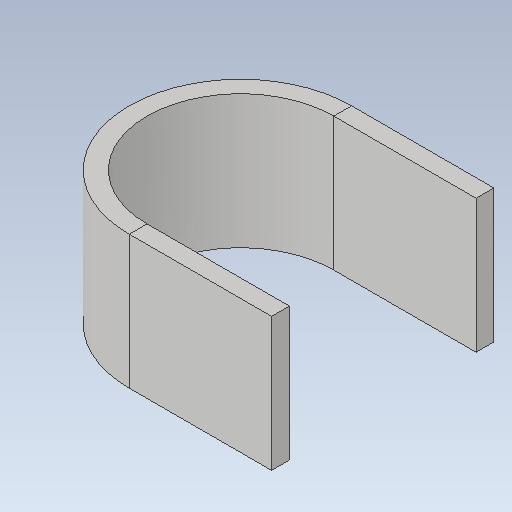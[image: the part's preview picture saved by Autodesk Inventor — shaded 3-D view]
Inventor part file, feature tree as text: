
AUTODESK INVENTOR PART (.ipt)
format: ipt  version: 2020.1 (Build 241239000, 239)  size: 136,704 bytes
history: native  units: mm
features: sheet_metal_op x3, other x2, sketch x1
ambient origin geometry x8: Origin, YZ Plane, XZ Plane, XY Plane, X Axis, Y Axis, Z Axis, Center Point
bodies: Solid1 (feature_tree)
feature tree (6):
  sheet_metal_op  "Contour Flange1"
  sketch  "Sketch1"  dims[d0=4.0mm d1=4.0mm d2=2.0mm d3=8.0mm d4=4.0mm d5=30.0mm d6=4.0mm d7=0.5mm d8=16.0mm d9=4.0mm d10=4.0mm d11=50.0mm d12=32.0mm]
  other  "Plate1"
  sheet_metal_op  "Bend1"
  sheet_metal_op  "Corner1"
  other  "Definition1"
